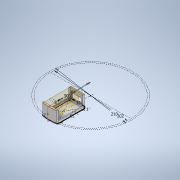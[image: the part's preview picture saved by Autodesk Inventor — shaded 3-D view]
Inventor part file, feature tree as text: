
AUTODESK INVENTOR PART (.ipt)
format: ipt  version: 2020 (Build 240168000, 168)  size: 232,960 bytes
history: native  units: mm
features: projected_geometry x12, extrude x6, sketch x5, other x3
ambient origin geometry x8: Origin, YZ Plane, XZ Plane, XY Plane, X Axis, Y Axis, Z Axis, Center Point
bodies: Body1 (feature_tree)
feature tree (26):
  other  "Твердое тело1"
  sketch  "Эскиз1"
  extrude  "Выдавливание3"  Depth=202.0mm
  other  "РабПлоскость1"
  extrude  "Выдавливание1"  Depth=35.0mm
  other  "РабПлоскость2"
  sketch  "Эскиз2"
  extrude  "Выдавливание4"  Depth=65.0mm
  extrude  "Выдавливание5"  Depth=2.0mm
  sketch  "Эскиз4"
  extrude  "Выдавливание6"  Depth=2.0mm
  extrude  "Выдавливание7"  Depth=3.0mm
  projected_geometry  "Спроецированная петля1"
  projected_geometry  "Спроецированная петля7"
  projected_geometry  "Спроецированная петля8"
  sketch  "Эскиз3"
  projected_geometry  "Спроецированная петля9"
  projected_geometry  "Спроецированная петля10"
  projected_geometry  "Спроецированная петля11"
  projected_geometry  "Спроецированная петля12"
  sketch  "Эскиз5"
  projected_geometry  "Спроецированная петля13"
  projected_geometry  "Спроецированная петля14"
  projected_geometry  "Спроецированная петля15"
  projected_geometry  "Спроецированная петля16"
  projected_geometry  "Спроецированная петля17"
